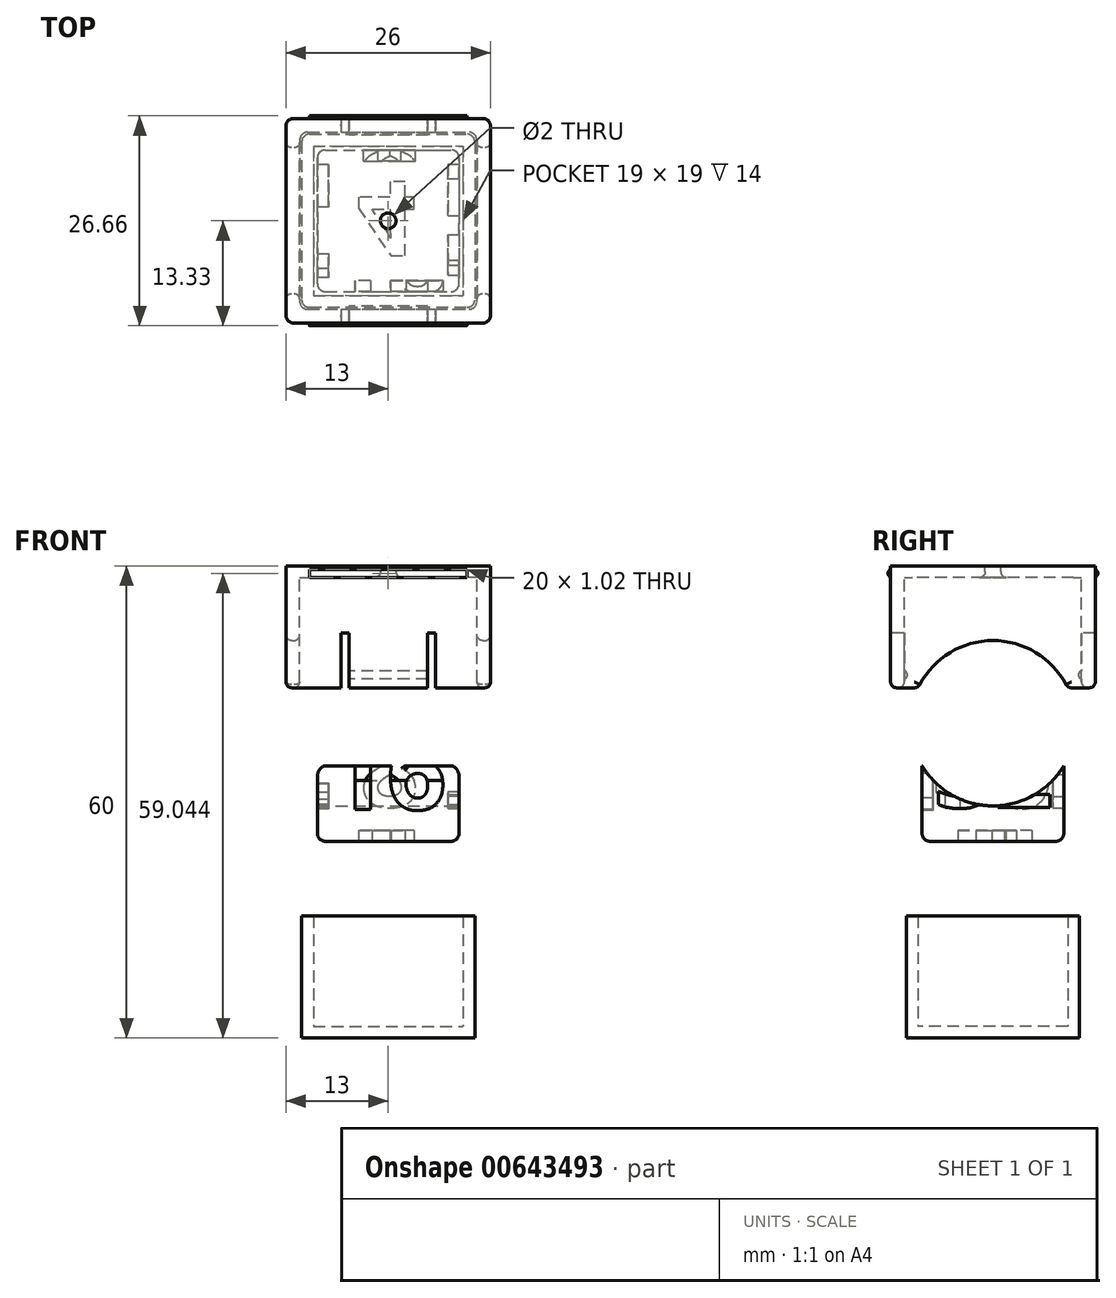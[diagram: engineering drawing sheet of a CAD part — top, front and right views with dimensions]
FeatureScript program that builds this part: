
annotation { "Feature Type Name" : "Feature", "Feature Type Description" : "" }
export const myFeature = defineFeature(function(context is Context, id is Id, definition is map)
    precondition{}
    {
        {
            var Q0;
            Q0=qCreatedBy(makeId("Top.planeOp"),FACE);
            var sketch = newSketch(context, id + "F0", { "sketchPlane" : qUnion([Q0])});
            skLineSegment(sketch, "E0.bottom", {"start": v(-9, 9) * mm, "end": v(9, 9) * mm});
            skLineSegment(sketch, "E0.top", {"start": v(-9, -9) * mm, "end": v(9, -9) * mm});
            skLineSegment(sketch, "E0.left", {"start": v(-9, 9) * mm, "end": v(-9, -9) * mm});
            skLineSegment(sketch, "E0.right", {"start": v(9, 9) * mm, "end": v(9, -9) * mm});
            skSolve(sketch);
        }
        {
            var Q0;
            Q0=makeQuery(id+"F0.imprint","IMPRINT",FACE,{"disambiguationData":[TD([[makeQuery(id+"F0.imprint","IMPRINT",EDGE,{"derivedFrom":sQuery(id+"F0.wireOp",EDGE,"E0.bottom")}),-1.0]])]});
            extrude(context, id + "F1", {"entities" : qUnion([Q0]), "depth" : 18 * mm, "offsetDistance" : 25 * mm});
        }
        {
            var Q0;
            Q0=makeQuery(id+"F1.opExtrude","CAP_FACE",FACE,{"disambiguationData":[OSD([sQuery(id+"F0.wireOp",EDGE,"E0.bottom"),sQuery(id+"F0.wireOp",EDGE,"E0.top"),sQuery(id+"F0.wireOp",EDGE,"E0.left"),sQuery(id+"F0.wireOp",EDGE,"E0.right")])],"isStart":false});
            var sketch = newSketch(context, id + "F2", { "sketchPlane" : qUnion([Q0])});
            skText(sketch, "E1", { "text": "2", "fontName": "Arimo-Bold.ttf"});
            const initialGuessF2  = {"E1": [-0.00386, -0.00431, 1, 0, 0.0095]};
            skSetInitialGuess(sketch, initialGuessF2);
            skSolve(sketch);
        }
        {
            var Q0;
            Q0 = qSketchRegion(id + "F2", true);
            extrude(context, id + "F3", {"entities" : qUnion([Q0]), "operationType" : NewBodyOperationType.REMOVE, "oppositeDirection" : true, "depth" : 1.4 * mm, "offsetDistance" : 25 * mm});
        }
        {
            var Q0;
            Q0=makeQuery(id+"F1.opExtrude","CAP_FACE",FACE,{"disambiguationData":[OSD([sQuery(id+"F0.wireOp",EDGE,"E0.bottom"),sQuery(id+"F0.wireOp",EDGE,"E0.top"),sQuery(id+"F0.wireOp",EDGE,"E0.left"),sQuery(id+"F0.wireOp",EDGE,"E0.right")])],"isStart":true});
            var sketch = newSketch(context, id + "F4", { "sketchPlane" : qUnion([Q0])});
            skText(sketch, "E2", { "text": "4", "fontName": "OpenSans-Bold.ttf"});
            const initialGuessF4  = {"E2": [-0.00403, -0.00496, 1, 0, 0.0095]};
            skSetInitialGuess(sketch, initialGuessF4);
            skSolve(sketch);
        }
        {
            var Q0;
            Q0=makeQuery(id+"F4.imprint","IMPRINT",FACE,{"disambiguationData":[TD([[makeQuery(id+"F4.imprint","IMPRINT",EDGE,{"derivedFrom":sQuery(id+"F4.wireOp",EDGE,"E2.sketch_text.stroke-0")}),-1.0]])]});
            extrude(context, id + "F5", {"entities" : qUnion([Q0]), "operationType" : NewBodyOperationType.REMOVE, "oppositeDirection" : true, "depth" : 1.4 * mm, "offsetDistance" : 25 * mm});
        }
        {
            var Q0;
            Q0=makeQuery(id+"F1.opExtrude","SWEPT_FACE",FACE,{"disambiguationData":[OSD([sQuery(id+"F0.wireOp",EDGE,"E0.bottom")])]});
            var sketch = newSketch(context, id + "F6", { "sketchPlane" : qUnion([Q0])});
            skText(sketch, "E3", { "text": "8", "fontName": "OpenSans-Bold.ttf"});
            const initialGuessF6  = {"E3": [-0.00393, 0.00436, 1, 0, 0.0095]};
            skSetInitialGuess(sketch, initialGuessF6);
            skSolve(sketch);
        }
        {
            var Q0;
            Q0 = qSketchRegion(id + "F6", true);
            extrude(context, id + "F7", {"entities" : qUnion([Q0]), "operationType" : NewBodyOperationType.REMOVE, "oppositeDirection" : true, "depth" : 1.4 * mm, "offsetDistance" : 25 * mm});
        }
        {
            var Q0;
            Q0=makeQuery(id+"F1.opExtrude","SWEPT_FACE",FACE,{"disambiguationData":[OSD([sQuery(id+"F0.wireOp",EDGE,"E0.top")])]});
            var sketch = newSketch(context, id + "F8", { "sketchPlane" : qUnion([Q0])});
            skText(sketch, "E4", { "text": "16", "fontName": "OpenSans-Bold.ttf"});
            const initialGuessF8  = {"E4": [-0.00771, 0.00402, 1, 0, 0.0095]};
            skSetInitialGuess(sketch, initialGuessF8);
            skSolve(sketch);
        }
        {
            var Q0;
            Q0 = qSketchRegion(id + "F8", true);
            extrude(context, id + "F9", {"entities" : qUnion([Q0]), "operationType" : NewBodyOperationType.REMOVE, "oppositeDirection" : true, "depth" : 1.4 * mm, "offsetDistance" : 25 * mm});
        }
        {
            var Q0;
            Q0=makeQuery(id+"F1.opExtrude","SWEPT_FACE",FACE,{"disambiguationData":[OSD([sQuery(id+"F0.wireOp",EDGE,"E0.right")])]});
            var sketch = newSketch(context, id + "F10", { "sketchPlane" : qUnion([Q0])});
            skText(sketch, "E5", { "text": "32", "fontName": "OpenSans-Bold.ttf"});
            const initialGuessF10  = {"E5": [-0.00743, 0.00428, 1, 0, 0.0095]};
            skSetInitialGuess(sketch, initialGuessF10);
            skSolve(sketch);
        }
        {
            var Q0;
            Q0 = qSketchRegion(id + "F10", true);
            extrude(context, id + "F11", {"entities" : qUnion([Q0]), "operationType" : NewBodyOperationType.REMOVE, "oppositeDirection" : true, "depth" : 1.4 * mm, "offsetDistance" : 25 * mm});
        }
        {
            var Q0;
            Q0=makeQuery(id+"F1.opExtrude","SWEPT_FACE",FACE,{"disambiguationData":[OSD([sQuery(id+"F0.wireOp",EDGE,"E0.left")])]});
            var sketch = newSketch(context, id + "F12", { "sketchPlane" : qUnion([Q0])});
            skText(sketch, "E6", { "text": "64", "fontName": "OpenSans-Bold.ttf"});
            const initialGuessF12  = {"E6": [-0.00763, 0.00423, 1, 0, 0.0095]};
            skSetInitialGuess(sketch, initialGuessF12);
            skSolve(sketch);
        }
        {
            var Q0;
            Q0 = qSketchRegion(id + "F12", true);
            extrude(context, id + "F13", {"entities" : qUnion([Q0]), "operationType" : NewBodyOperationType.REMOVE, "oppositeDirection" : true, "depth" : 1.4 * mm, "offsetDistance" : 25 * mm});
        }
        {
            var Q0;
            Q0=makeQuery(id+"F1.opExtrude","CAP_EDGE",EDGE,{"disambiguationData":[OSD([sQuery(id+"F0.wireOp",EDGE,"E0.right")])],"isStart":false});
            var Q1;
            Q1=makeQuery(id+"F1.opExtrude","CAP_EDGE",EDGE,{"disambiguationData":[OSD([sQuery(id+"F0.wireOp",EDGE,"E0.bottom")])],"isStart":false});
            var Q2;
            Q2=makeQuery(id+"F1.opExtrude","SWEPT_EDGE",EDGE,{"disambiguationData":[OSD([sQuery(id+"F0.wireOp",EDGE,"E0.bottom"),sQuery(id+"F0.wireOp",EDGE,"E0.right")])]});
            var Q3;
            Q3=makeQuery(id+"F1.opExtrude","SWEPT_EDGE",EDGE,{"disambiguationData":[OSD([sQuery(id+"F0.wireOp",EDGE,"E0.bottom"),sQuery(id+"F0.wireOp",EDGE,"E0.left")])]});
            var Q4;
            Q4=makeQuery(id+"F1.opExtrude","CAP_EDGE",EDGE,{"disambiguationData":[OSD([sQuery(id+"F0.wireOp",EDGE,"E0.left")])],"isStart":false});
            var Q5;
            Q5=makeQuery(id+"F1.opExtrude","CAP_EDGE",EDGE,{"disambiguationData":[OSD([sQuery(id+"F0.wireOp",EDGE,"E0.top")])],"isStart":false});
            var Q6;
            Q6=makeQuery(id+"F1.opExtrude","SWEPT_EDGE",EDGE,{"disambiguationData":[OSD([sQuery(id+"F0.wireOp",EDGE,"E0.top"),sQuery(id+"F0.wireOp",EDGE,"E0.right")])]});
            var Q7;
            Q7=makeQuery(id+"F1.opExtrude","CAP_EDGE",EDGE,{"disambiguationData":[OSD([sQuery(id+"F0.wireOp",EDGE,"E0.right")])],"isStart":true});
            var Q8;
            Q8=makeQuery(id+"F1.opExtrude","CAP_EDGE",EDGE,{"disambiguationData":[OSD([sQuery(id+"F0.wireOp",EDGE,"E0.top")])],"isStart":true});
            var Q9;
            Q9=makeQuery(id+"F1.opExtrude","SWEPT_EDGE",EDGE,{"disambiguationData":[OSD([sQuery(id+"F0.wireOp",EDGE,"E0.top"),sQuery(id+"F0.wireOp",EDGE,"E0.left")])]});
            var Q10;
            Q10=makeQuery(id+"F1.opExtrude","CAP_EDGE",EDGE,{"disambiguationData":[OSD([sQuery(id+"F0.wireOp",EDGE,"E0.left")])],"isStart":true});
            var Q11;
            Q11=makeQuery(id+"F1.opExtrude","CAP_EDGE",EDGE,{"disambiguationData":[OSD([sQuery(id+"F0.wireOp",EDGE,"E0.bottom")])],"isStart":true});
            fillet(context, id + "F14", {"entities" : qUnion([Q0, Q1, Q2, Q3, Q4, Q5, Q6, Q7, Q8, Q9, Q10, Q11]), "radius" : 1 * mm, "tangentPropagation" : true, "allowEdgeOverflow" : false});
        }
        {
            var Q0;
            Q0=qCreatedBy(makeId("Top.planeOp"),FACE);
            cPlane(context, id + "F15", {"entities" : qUnion([Q0]), "cplaneType" : CPlaneType.OFFSET, "offset" : 25 * mm, "oppositeDirection" : true, "width" : 150 * mm, "height" : 150 * mm});
        }
        {
            var Q0;
            Q0=qCreatedBy(id+"F15.planeOp",FACE);
            var sketch = newSketch(context, id + "F16", { "sketchPlane" : qUnion([Q0])});
            skLineSegment(sketch, "E7.bottom", {"start": v(-11, 11) * mm, "end": v(11, 11) * mm});
            skLineSegment(sketch, "E7.top", {"start": v(-11, -11) * mm, "end": v(11, -11) * mm});
            skLineSegment(sketch, "E7.left", {"start": v(-11, 11) * mm, "end": v(-11, -11) * mm});
            skLineSegment(sketch, "E7.right", {"start": v(11, 11) * mm, "end": v(11, -11) * mm});
            skSolve(sketch);
        }
        {
            var Q0;
            Q0 = qSketchRegion(id + "F16", true);
            extrude(context, id + "F17", {"entities" : qUnion([Q0]), "depth" : 1.5 * mm, "offsetDistance" : 25 * mm});
        }
        {
            var Q0;
            Q0=makeQuery(id+"F17.opExtrude","CAP_FACE",FACE,{"disambiguationData":[OSD([sQuery(id+"F16.wireOp",EDGE,"E7.bottom"),sQuery(id+"F16.wireOp",EDGE,"E7.top"),sQuery(id+"F16.wireOp",EDGE,"E7.left"),sQuery(id+"F16.wireOp",EDGE,"E7.right")])],"isStart":false});
            var sketch = newSketch(context, id + "F18", { "sketchPlane" : qUnion([Q0])});
            skLineSegment(sketch, "E8.bottom", {"start": v(-11, 11) * mm, "end": v(11, 11) * mm});
            skLineSegment(sketch, "E8.top", {"start": v(-11, -11) * mm, "end": v(11, -11) * mm});
            skLineSegment(sketch, "E8.left", {"start": v(-11, 11) * mm, "end": v(-11, -11) * mm});
            skLineSegment(sketch, "E8.right", {"start": v(11, 11) * mm, "end": v(11, -11) * mm});
            skLineSegment(sketch, "E9.bottom", {"start": v(-9.5, 9.5) * mm, "end": v(9.5, 9.5) * mm});
            skLineSegment(sketch, "E9.top", {"start": v(-9.5, -9.5) * mm, "end": v(9.5, -9.5) * mm});
            skLineSegment(sketch, "E9.left", {"start": v(-9.5, 9.5) * mm, "end": v(-9.5, -9.5) * mm});
            skLineSegment(sketch, "E9.right", {"start": v(9.5, 9.5) * mm, "end": v(9.5, -9.5) * mm});
            skSolve(sketch);
        }
        {
            var Q0;
            Q0 = qSketchRegion(id + "F18", true);
            extrude(context, id + "F19", {"entities" : qUnion([Q0]), "operationType" : NewBodyOperationType.ADD, "depth" : 14 * mm, "offsetDistance" : 25 * mm});
        }
        {
            var Q0;
            Q0=makeQuery(id+"F19.boolean.opBoolean","MERGE",EDGE,{"derivedFrom":[makeQuery(id+"F17.opExtrude","SWEPT_EDGE",EDGE,{"disambiguationData":[OSD([sQuery(id+"F16.wireOp",EDGE,"E7.bottom"),sQuery(id+"F16.wireOp",EDGE,"E7.left")])]}),makeQuery(id+"F19.opExtrude","SWEPT_EDGE",EDGE,{"disambiguationData":[OSD([sQuery(id+"F18.wireOp",EDGE,"E8.bottom"),sQuery(id+"F18.wireOp",EDGE,"E8.left")])]})]});
            var Q1;
            Q1=makeQuery(id+"F19.boolean.opBoolean","MERGE",EDGE,{"derivedFrom":[makeQuery(id+"F17.opExtrude","SWEPT_EDGE",EDGE,{"disambiguationData":[OSD([sQuery(id+"F16.wireOp",EDGE,"E7.bottom"),sQuery(id+"F16.wireOp",EDGE,"E7.right")])]}),makeQuery(id+"F19.opExtrude","SWEPT_EDGE",EDGE,{"disambiguationData":[OSD([sQuery(id+"F18.wireOp",EDGE,"E8.bottom"),sQuery(id+"F18.wireOp",EDGE,"E8.right")])]})]});
            var Q2;
            Q2=makeQuery(id+"F19.boolean.opBoolean","MERGE",EDGE,{"derivedFrom":[makeQuery(id+"F17.opExtrude","SWEPT_EDGE",EDGE,{"disambiguationData":[OSD([sQuery(id+"F16.wireOp",EDGE,"E7.top"),sQuery(id+"F16.wireOp",EDGE,"E7.right")])]}),makeQuery(id+"F19.opExtrude","SWEPT_EDGE",EDGE,{"disambiguationData":[OSD([sQuery(id+"F18.wireOp",EDGE,"E8.top"),sQuery(id+"F18.wireOp",EDGE,"E8.right")])]})]});
            var Q3;
            Q3=makeQuery(id+"F19.boolean.opBoolean","MERGE",EDGE,{"derivedFrom":[makeQuery(id+"F17.opExtrude","SWEPT_EDGE",EDGE,{"disambiguationData":[OSD([sQuery(id+"F16.wireOp",EDGE,"E7.top"),sQuery(id+"F16.wireOp",EDGE,"E7.left")])]}),makeQuery(id+"F19.opExtrude","SWEPT_EDGE",EDGE,{"disambiguationData":[OSD([sQuery(id+"F18.wireOp",EDGE,"E8.top"),sQuery(id+"F18.wireOp",EDGE,"E8.left")])]})]});
            fillet(context, id + "F20", {"entities" : qUnion([Q0, Q1, Q2, Q3]), "radius" : 1 * mm, "tangentPropagation" : true, "allowEdgeOverflow" : false});
        }
        {
            var Q0;
            Q0=qCreatedBy(makeId("Top.planeOp"),FACE);
            cPlane(context, id + "F21", {"entities" : qUnion([Q0]), "cplaneType" : CPlaneType.OFFSET, "offset" : 35 * mm, "width" : 150 * mm, "height" : 150 * mm});
        }
        {
            var Q0;
            Q0=qCreatedBy(id+"F21.planeOp",FACE);
            var sketch = newSketch(context, id + "F22", { "sketchPlane" : qUnion([Q0])});
            skLineSegment(sketch, "E10.bottom", {"start": v(-13, 13) * mm, "end": v(13, 13) * mm});
            skLineSegment(sketch, "E10.top", {"start": v(-13, -13) * mm, "end": v(13, -13) * mm});
            skLineSegment(sketch, "E10.left", {"start": v(-13, 13) * mm, "end": v(-13, -13) * mm});
            skLineSegment(sketch, "E10.right", {"start": v(13, 13) * mm, "end": v(13, -13) * mm});
            skSolve(sketch);
        }
        {
            var Q0;
            Q0 = qSketchRegion(id + "F22", true);
            extrude(context, id + "F23", {"entities" : qUnion([Q0]), "oppositeDirection" : true, "depth" : 1.5 * mm, "offsetDistance" : 25 * mm});
        }
        {
            var Q0;
            Q0=makeQuery(id+"F23.opExtrude","CAP_FACE",FACE,{"disambiguationData":[OSD([sQuery(id+"F22.wireOp",EDGE,"E10.bottom"),sQuery(id+"F22.wireOp",EDGE,"E10.top"),sQuery(id+"F22.wireOp",EDGE,"E10.left"),sQuery(id+"F22.wireOp",EDGE,"E10.right")])],"isStart":false});
            var sketch = newSketch(context, id + "F24", { "sketchPlane" : qUnion([Q0])});
            skLineSegment(sketch, "E11.bottom", {"start": v(-13, -13) * mm, "end": v(13, -13) * mm});
            skLineSegment(sketch, "E11.top", {"start": v(-13, 13) * mm, "end": v(13, 13) * mm});
            skLineSegment(sketch, "E11.left", {"start": v(-13, -13) * mm, "end": v(-13, 13) * mm});
            skLineSegment(sketch, "E11.right", {"start": v(13, -13) * mm, "end": v(13, 13) * mm});
            skLineSegment(sketch, "E12.bottom", {"start": v(-11.25, -11.25) * mm, "end": v(11.25, -11.25) * mm});
            skLineSegment(sketch, "E12.top", {"start": v(-11.25, 11.25) * mm, "end": v(11.25, 11.25) * mm});
            skLineSegment(sketch, "E12.left", {"start": v(-11.25, -11.25) * mm, "end": v(-11.25, 11.25) * mm});
            skLineSegment(sketch, "E12.right", {"start": v(11.25, -11.25) * mm, "end": v(11.25, 11.25) * mm});
            skSolve(sketch);
        }
        {
            var Q0;
            Q0 = qSketchRegion(id + "F24", true);
            extrude(context, id + "F25", {"entities" : qUnion([Q0]), "operationType" : NewBodyOperationType.ADD, "depth" : 14 * mm, "offsetDistance" : 25 * mm});
        }
        {
            var Q0;
            Q0=makeQuery(id+"F25.opExtrude","SWEPT_EDGE",EDGE,{"disambiguationData":[OSD([sQuery(id+"F24.wireOp",EDGE,"E12.top"),sQuery(id+"F24.wireOp",EDGE,"E12.left")])]});
            var Q1;
            Q1=makeQuery(id+"F25.opExtrude","SWEPT_EDGE",EDGE,{"disambiguationData":[OSD([sQuery(id+"F24.wireOp",EDGE,"E12.top"),sQuery(id+"F24.wireOp",EDGE,"E12.right")])]});
            var Q2;
            Q2=makeQuery(id+"F25.opExtrude","SWEPT_EDGE",EDGE,{"disambiguationData":[OSD([sQuery(id+"F24.wireOp",EDGE,"E12.bottom"),sQuery(id+"F24.wireOp",EDGE,"E12.left")])]});
            var Q3;
            Q3=makeQuery(id+"F25.opExtrude","SWEPT_EDGE",EDGE,{"disambiguationData":[OSD([sQuery(id+"F24.wireOp",EDGE,"E12.bottom"),sQuery(id+"F24.wireOp",EDGE,"E12.right")])]});
            var Q4;
            Q4=makeQuery(id+"F25.boolean.opBoolean","MERGE",EDGE,{"derivedFrom":[makeQuery(id+"F23.opExtrude","SWEPT_EDGE",EDGE,{"disambiguationData":[OSD([sQuery(id+"F22.wireOp",EDGE,"E10.top"),sQuery(id+"F22.wireOp",EDGE,"E10.right")])]}),makeQuery(id+"F25.opExtrude","SWEPT_EDGE",EDGE,{"disambiguationData":[OSD([sQuery(id+"F24.wireOp",EDGE,"E11.top"),sQuery(id+"F24.wireOp",EDGE,"E11.right")])]})]});
            var Q5;
            Q5=makeQuery(id+"F25.boolean.opBoolean","MERGE",EDGE,{"derivedFrom":[makeQuery(id+"F23.opExtrude","SWEPT_EDGE",EDGE,{"disambiguationData":[OSD([sQuery(id+"F22.wireOp",EDGE,"E10.top"),sQuery(id+"F22.wireOp",EDGE,"E10.left")])]}),makeQuery(id+"F25.opExtrude","SWEPT_EDGE",EDGE,{"disambiguationData":[OSD([sQuery(id+"F24.wireOp",EDGE,"E11.top"),sQuery(id+"F24.wireOp",EDGE,"E11.left")])]})]});
            var Q6;
            Q6=makeQuery(id+"F25.boolean.opBoolean","MERGE",EDGE,{"derivedFrom":[makeQuery(id+"F23.opExtrude","SWEPT_EDGE",EDGE,{"disambiguationData":[OSD([sQuery(id+"F22.wireOp",EDGE,"E10.bottom"),sQuery(id+"F22.wireOp",EDGE,"E10.left")])]}),makeQuery(id+"F25.opExtrude","SWEPT_EDGE",EDGE,{"disambiguationData":[OSD([sQuery(id+"F24.wireOp",EDGE,"E11.bottom"),sQuery(id+"F24.wireOp",EDGE,"E11.left")])]})]});
            var Q7;
            Q7=makeQuery(id+"F25.boolean.opBoolean","MERGE",EDGE,{"derivedFrom":[makeQuery(id+"F23.opExtrude","SWEPT_EDGE",EDGE,{"disambiguationData":[OSD([sQuery(id+"F22.wireOp",EDGE,"E10.bottom"),sQuery(id+"F22.wireOp",EDGE,"E10.right")])]}),makeQuery(id+"F25.opExtrude","SWEPT_EDGE",EDGE,{"disambiguationData":[OSD([sQuery(id+"F24.wireOp",EDGE,"E11.bottom"),sQuery(id+"F24.wireOp",EDGE,"E11.right")])]})]});
            fillet(context, id + "F26", {"entities" : qUnion([Q0, Q1, Q2, Q3, Q4, Q5, Q6, Q7]), "radius" : 1 * mm, "tangentPropagation" : true, "allowEdgeOverflow" : false});
        }
        {
            var Q0;
            Q0=qCreatedBy(makeId("Right.planeOp"),FACE);
            var sketch = newSketch(context, id + "F27", { "sketchPlane" : qUnion([Q0])});
            skCircle(sketch, "E13", {"center": v(0, 15) * mm, "radius": 10.5 * mm});
            skSolve(sketch);
        }
        {
            var Q0;
            Q0 = qSketchRegion(id + "F27", true);
            extrude(context, id + "F28", {"entities" : qUnion([Q0]), "operationType" : NewBodyOperationType.REMOVE, "endBound" : BoundingType.SYMMETRIC, "oppositeDirection" : true, "depth" : 30 * mm, "offsetDistance" : 25 * mm});
        }
        {
            var Q0;
            Q0=makeQuery(id+"F28.boolean.opBoolean","INTERSECT",EDGE,{"derivedFrom":[makeQuery(id+"F25.boolean.opBoolean","MERGE",FACE,{"derivedFrom":[makeQuery(id+"F23.opExtrude","SWEPT_FACE",FACE,{"disambiguationData":[OSD([sQuery(id+"F22.wireOp",EDGE,"E10.right")])]}),makeQuery(id+"F25.opExtrude","SWEPT_FACE",FACE,{"disambiguationData":[OSD([sQuery(id+"F24.wireOp",EDGE,"E11.right")])]})]}),makeQuery(id+"F28.opExtrude","SWEPT_FACE",FACE,{"disambiguationData":[OSD([sQuery(id+"F27.wireOp",EDGE,"E13")])]})]});
            var Q1;
            Q1=makeQuery(id+"F28.boolean.opBoolean","INTERSECT",EDGE,{"derivedFrom":[makeQuery(id+"F25.opExtrude","SWEPT_FACE",FACE,{"disambiguationData":[OSD([sQuery(id+"F24.wireOp",EDGE,"E12.right")])]}),makeQuery(id+"F28.opExtrude","SWEPT_FACE",FACE,{"disambiguationData":[OSD([sQuery(id+"F27.wireOp",EDGE,"E13")])]})]});
            var Q2;
            Q2=makeQuery(id+"F28.boolean.opBoolean","INTERSECT",EDGE,{"derivedFrom":[makeQuery(id+"F25.boolean.opBoolean","MERGE",FACE,{"derivedFrom":[makeQuery(id+"F23.opExtrude","SWEPT_FACE",FACE,{"disambiguationData":[OSD([sQuery(id+"F22.wireOp",EDGE,"E10.left")])]}),makeQuery(id+"F25.opExtrude","SWEPT_FACE",FACE,{"disambiguationData":[OSD([sQuery(id+"F24.wireOp",EDGE,"E11.left")])]})]}),makeQuery(id+"F28.opExtrude","SWEPT_FACE",FACE,{"disambiguationData":[OSD([sQuery(id+"F27.wireOp",EDGE,"E13")])]})]});
            var Q3;
            Q3=makeQuery(id+"F28.boolean.opBoolean","INTERSECT",EDGE,{"derivedFrom":[makeQuery(id+"F25.opExtrude","SWEPT_FACE",FACE,{"disambiguationData":[OSD([sQuery(id+"F24.wireOp",EDGE,"E12.left")])]}),makeQuery(id+"F28.opExtrude","SWEPT_FACE",FACE,{"disambiguationData":[OSD([sQuery(id+"F27.wireOp",EDGE,"E13")])]})]});
            fillet(context, id + "F29", {"entities" : qUnion([Q0, Q1, Q2, Q3]), "radius" : 0.74 * mm, "tangentPropagation" : true, "allowEdgeOverflow" : false});
        }
        {
            var Q0;
            Q0=makeQuery(id+"F23.opExtrude","CAP_FACE",FACE,{"disambiguationData":[OSD([sQuery(id+"F22.wireOp",EDGE,"E10.bottom"),sQuery(id+"F22.wireOp",EDGE,"E10.top"),sQuery(id+"F22.wireOp",EDGE,"E10.left"),sQuery(id+"F22.wireOp",EDGE,"E10.right")])],"isStart":true});
            var sketch = newSketch(context, id + "F30", { "sketchPlane" : qUnion([Q0])});
            skCircle(sketch, "E14", {"center": v(0, 0) * mm, "radius": 1 * mm});
            skSolve(sketch);
        }
        {
            var Q0;
            Q0 = qSketchRegion(id + "F30", true);
            extrude(context, id + "F31", {"entities" : qUnion([Q0]), "operationType" : NewBodyOperationType.REMOVE, "oppositeDirection" : true, "depth" : 3 * mm, "offsetDistance" : 25 * mm});
        }
        {
            var Q0;
            Q0=qCreatedBy(makeId("Right.planeOp"),FACE);
            var sketch = newSketch(context, id + "F32", { "sketchPlane" : qUnion([Q0])});
            skArc(sketch, "E15", {"start": v(11.25, 21.63) * mm, "mid": v(10.85, 21.13) * mm, "end": v(11.25, 20.62) * mm});
            skLineSegment(sketch, "E16", {"start": v(11.25, 17.44) * mm, "end": v(11.25, 26.73) * mm, "construction": true});
            skLineSegment(sketch, "E17", {"start": v(11.25, 21.63) * mm, "end": v(11.25, 20.62) * mm});
            skSolve(sketch);
        }
        {
            var Q0;
            Q0 = qSketchRegion(id + "F32", true);
            extrude(context, id + "F33", {"entities" : qUnion([Q0]), "endBound" : BoundingType.SYMMETRIC, "depth" : 10 * mm, "offsetDistance" : 25 * mm});
        }
        {
            var Q0;
            Q0=makeQuery(id+"F33.opExtrude","SWEPT_BODY",BODY,{"disambiguationData":[OSD([sQuery(id+"F32.wireOp",EDGE,"E15"),sQuery(id+"F32.wireOp",EDGE,"E17")])]});
            var Q1;
            Q1=qCreatedBy(makeId("Front.planeOp"),FACE);
            mirror(context, id + "F34", {"operationType" : NewBodyOperationType.ADD, "entities" : qUnion([Q0]), "mirrorPlane" : qUnion([Q1])});
        }
        {
            var Q0;
            Q0=makeQuery(id+"F25.opExtrude","SWEPT_FACE",FACE,{"disambiguationData":[OSD([sQuery(id+"F24.wireOp",EDGE,"E12.top")])]});
            var sketch = newSketch(context, id + "F35", { "sketchPlane" : qUnion([Q0])});
            skLineSegment(sketch, "E18.bottom", {"start": v(-5, 16.34) * mm, "end": v(-6, 16.34) * mm});
            skLineSegment(sketch, "E18.top", {"start": v(-5, 26.45) * mm, "end": v(-6, 26.45) * mm});
            skLineSegment(sketch, "E18.left", {"start": v(-5, 16.34) * mm, "end": v(-5, 26.45) * mm});
            skLineSegment(sketch, "E18.right", {"start": v(-6, 16.34) * mm, "end": v(-6, 26.45) * mm});
            skSolve(sketch);
        }
        {
            var Q0;
            Q0 = qSketchRegion(id + "F35", true);
            extrude(context, id + "F36", {"entities" : qUnion([Q0]), "endBound" : BoundingType.SYMMETRIC, "depth" : 50 * mm, "offsetDistance" : 25 * mm});
        }
        {
            var Q0;
            Q0=makeQuery(id+"F36.opExtrude","SWEPT_BODY",BODY,{"disambiguationData":[OSD([sQuery(id+"F35.wireOp",EDGE,"E18.bottom"),sQuery(id+"F35.wireOp",EDGE,"E18.top"),sQuery(id+"F35.wireOp",EDGE,"E18.left"),sQuery(id+"F35.wireOp",EDGE,"E18.right")])]});
            var Q1;
            Q1=qCreatedBy(makeId("Right.planeOp"),FACE);
            mirror(context, id + "F37", {"entities" : qUnion([Q0]), "mirrorPlane" : qUnion([Q1])});
        }
        {
            var Q0;
            Q0=makeQuery(id+"F36.opExtrude","SWEPT_BODY",BODY,{"disambiguationData":[OSD([sQuery(id+"F35.wireOp",EDGE,"E18.bottom"),sQuery(id+"F35.wireOp",EDGE,"E18.top"),sQuery(id+"F35.wireOp",EDGE,"E18.left"),sQuery(id+"F35.wireOp",EDGE,"E18.right")])]});
            var Q1;
            Q1=makeQuery(id+"F37.opPattern","COPY",BODY,{"derivedFrom":makeQuery(id+"F36.opExtrude","SWEPT_BODY",BODY,{"disambiguationData":[OSD([sQuery(id+"F35.wireOp",EDGE,"E18.bottom"),sQuery(id+"F35.wireOp",EDGE,"E18.top"),sQuery(id+"F35.wireOp",EDGE,"E18.left"),sQuery(id+"F35.wireOp",EDGE,"E18.right")])]}),"instanceName":"1"});
            var Q2;
            Q2=makeQuery(id+"F23.opExtrude","SWEPT_BODY",BODY,{"disambiguationData":[OSD([sQuery(id+"F22.wireOp",EDGE,"E10.bottom"),sQuery(id+"F22.wireOp",EDGE,"E10.top"),sQuery(id+"F22.wireOp",EDGE,"E10.left"),sQuery(id+"F22.wireOp",EDGE,"E10.right")])]});
            booleanBodies(context, id + "F38", {"operationType" : BooleanOperationType.SUBTRACTION, "tools" : qUnion([Q0, Q1]), "targets" : qUnion([Q2])});
        }
        {
            var Q0;
            Q0=qCreatedBy(makeId("Right.planeOp"),FACE);
            var sketch = newSketch(context, id + "F39", { "sketchPlane" : qUnion([Q0])});
            skArc(sketch, "E19", {"start": v(-13, 34.55) * mm, "mid": v(-13.33, 34.04) * mm, "end": v(-13, 33.54) * mm});
            skLineSegment(sketch, "E20", {"start": v(-13, 36) * mm, "end": v(-13, 28.95) * mm, "construction": true});
            skLineSegment(sketch, "E21", {"start": v(-13, 34.55) * mm, "end": v(-13, 33.54) * mm});
            skSolve(sketch);
        }
        {
            var Q0;
            Q0 = qSketchRegion(id + "F39", true);
            extrude(context, id + "F40", {"entities" : qUnion([Q0]), "endBound" : BoundingType.SYMMETRIC, "depth" : 20 * mm, "offsetDistance" : 25 * mm});
        }
        {
            var Q0;
            Q0=makeQuery(id+"F40.opExtrude","SWEPT_BODY",BODY,{"disambiguationData":[OSD([sQuery(id+"F39.wireOp",EDGE,"E19"),sQuery(id+"F39.wireOp",EDGE,"E21")])]});
            var Q1;
            Q1=qCreatedBy(makeId("Front.planeOp"),FACE);
            mirror(context, id + "F41", {"operationType" : NewBodyOperationType.ADD, "entities" : qUnion([Q0]), "mirrorPlane" : qUnion([Q1])});
        }
        {
            var Q0;
            {var subQ0=sQuery(id+"F24.wireOp",EDGE,"E12.left");var subQ1=sQuery(id+"F24.wireOp",EDGE,"E12.bottom");Q0=makeQuery(id+"F26.opFillet","BLEND_EDGE",EDGE,{"blendedFrom":[makeQuery(id+"F25.opExtrude","SWEPT_EDGE",EDGE,{"disambiguationData":[OSD([subQ1,subQ0])]}),makeQuery(id+"F25.opExtrude","CAP_FACE",FACE,{"disambiguationData":[OSD([sQuery(id+"F24.wireOp",EDGE,"E11.bottom"),sQuery(id+"F24.wireOp",EDGE,"E11.top"),sQuery(id+"F24.wireOp",EDGE,"E11.left"),sQuery(id+"F24.wireOp",EDGE,"E11.right"),subQ1,sQuery(id+"F24.wireOp",EDGE,"E12.top"),subQ0,sQuery(id+"F24.wireOp",EDGE,"E12.right")])],"isStart":false})],"blendedInto":[makeQuery(id+"F25.opExtrude","CAP_FACE",FACE,{"disambiguationData":[OSD([sQuery(id+"F24.wireOp",EDGE,"E11.bottom"),sQuery(id+"F24.wireOp",EDGE,"E11.top"),sQuery(id+"F24.wireOp",EDGE,"E11.left"),sQuery(id+"F24.wireOp",EDGE,"E11.right"),subQ1,sQuery(id+"F24.wireOp",EDGE,"E12.top"),subQ0,sQuery(id+"F24.wireOp",EDGE,"E12.right")])],"isStart":false})]});}
            var Q1;
            {var subQ2=sQuery(id+"F24.wireOp",EDGE,"E12.bottom");var subQ3=makeQuery(id+"F36.opExtrude","SWEPT_FACE",FACE,{"disambiguationData":[OSD([sQuery(id+"F35.wireOp",EDGE,"E18.left")])]});Q1=makeQuery(id+"F38.opBoolean","SPLIT",EDGE,{"disambiguationData":[TD([subQ3])],"derivedFrom":makeQuery(id+"F25.opExtrude","CAP_EDGE",EDGE,{"disambiguationData":[OSD([subQ2])],"isStart":false})});}
            var Q2;
            {var subQ2=sQuery(id+"F24.wireOp",EDGE,"E11.bottom");var subQ3=makeQuery(id+"F36.opExtrude","SWEPT_FACE",FACE,{"disambiguationData":[OSD([sQuery(id+"F35.wireOp",EDGE,"E18.left")])]});Q2=makeQuery(id+"F38.opBoolean","SPLIT",EDGE,{"disambiguationData":[TD([subQ3])],"derivedFrom":makeQuery(id+"F25.opExtrude","CAP_EDGE",EDGE,{"disambiguationData":[OSD([subQ2])],"isStart":false})});}
            var Q3;
            {var subQ0=sQuery(id+"F24.wireOp",EDGE,"E11.bottom");Q3=makeQuery(id+"F38.opBoolean","SPLIT",EDGE,{"disambiguationData":[TD([makeQuery(id+"F36.opExtrude","SWEPT_FACE",FACE,{"disambiguationData":[OSD([sQuery(id+"F35.wireOp",EDGE,"E18.right")])]})])],"derivedFrom":makeQuery(id+"F25.opExtrude","CAP_EDGE",EDGE,{"disambiguationData":[OSD([subQ0])],"isStart":false})});}
            var Q4;
            {var subQ0=sQuery(id+"F24.wireOp",EDGE,"E12.right");var subQ1=sQuery(id+"F24.wireOp",EDGE,"E12.top");Q4=makeQuery(id+"F26.opFillet","BLEND_EDGE",EDGE,{"blendedFrom":[makeQuery(id+"F25.opExtrude","SWEPT_EDGE",EDGE,{"disambiguationData":[OSD([subQ1,subQ0])]}),makeQuery(id+"F25.opExtrude","CAP_FACE",FACE,{"disambiguationData":[OSD([sQuery(id+"F24.wireOp",EDGE,"E11.bottom"),sQuery(id+"F24.wireOp",EDGE,"E11.top"),sQuery(id+"F24.wireOp",EDGE,"E11.left"),sQuery(id+"F24.wireOp",EDGE,"E11.right"),sQuery(id+"F24.wireOp",EDGE,"E12.bottom"),subQ1,sQuery(id+"F24.wireOp",EDGE,"E12.left"),subQ0])],"isStart":false})],"blendedInto":[makeQuery(id+"F25.opExtrude","CAP_FACE",FACE,{"disambiguationData":[OSD([sQuery(id+"F24.wireOp",EDGE,"E11.bottom"),sQuery(id+"F24.wireOp",EDGE,"E11.top"),sQuery(id+"F24.wireOp",EDGE,"E11.left"),sQuery(id+"F24.wireOp",EDGE,"E11.right"),sQuery(id+"F24.wireOp",EDGE,"E12.bottom"),subQ1,sQuery(id+"F24.wireOp",EDGE,"E12.left"),subQ0])],"isStart":false})]});}
            var Q5;
            {var subQ2=sQuery(id+"F24.wireOp",EDGE,"E11.top");var subQ3=makeQuery(id+"F36.opExtrude","SWEPT_FACE",FACE,{"disambiguationData":[OSD([sQuery(id+"F35.wireOp",EDGE,"E18.left")])]});Q5=makeQuery(id+"F38.opBoolean","SPLIT",EDGE,{"disambiguationData":[TD([subQ3])],"derivedFrom":makeQuery(id+"F25.opExtrude","CAP_EDGE",EDGE,{"disambiguationData":[OSD([subQ2])],"isStart":false})});}
            var Q6;
            {var subQ0=sQuery(id+"F24.wireOp",EDGE,"E12.left");var subQ1=sQuery(id+"F24.wireOp",EDGE,"E12.top");Q6=makeQuery(id+"F26.opFillet","BLEND_EDGE",EDGE,{"blendedFrom":[makeQuery(id+"F25.opExtrude","SWEPT_EDGE",EDGE,{"disambiguationData":[OSD([subQ1,subQ0])]}),makeQuery(id+"F25.opExtrude","CAP_FACE",FACE,{"disambiguationData":[OSD([sQuery(id+"F24.wireOp",EDGE,"E11.bottom"),sQuery(id+"F24.wireOp",EDGE,"E11.top"),sQuery(id+"F24.wireOp",EDGE,"E11.left"),sQuery(id+"F24.wireOp",EDGE,"E11.right"),sQuery(id+"F24.wireOp",EDGE,"E12.bottom"),subQ1,subQ0,sQuery(id+"F24.wireOp",EDGE,"E12.right")])],"isStart":false})],"blendedInto":[makeQuery(id+"F25.opExtrude","CAP_FACE",FACE,{"disambiguationData":[OSD([sQuery(id+"F24.wireOp",EDGE,"E11.bottom"),sQuery(id+"F24.wireOp",EDGE,"E11.top"),sQuery(id+"F24.wireOp",EDGE,"E11.left"),sQuery(id+"F24.wireOp",EDGE,"E11.right"),sQuery(id+"F24.wireOp",EDGE,"E12.bottom"),subQ1,subQ0,sQuery(id+"F24.wireOp",EDGE,"E12.right")])],"isStart":false})]});}
            var Q7;
            {var subQ2=sQuery(id+"F24.wireOp",EDGE,"E12.top");var subQ3=makeQuery(id+"F36.opExtrude","SWEPT_FACE",FACE,{"disambiguationData":[OSD([sQuery(id+"F35.wireOp",EDGE,"E18.left")])]});Q7=makeQuery(id+"F38.opBoolean","SPLIT",EDGE,{"disambiguationData":[TD([subQ3])],"derivedFrom":makeQuery(id+"F25.opExtrude","CAP_EDGE",EDGE,{"disambiguationData":[OSD([subQ2])],"isStart":false})});}
            var Q8;
            Q8=makeQuery(id+"F31.boolean.opBoolean","INTERSECT",EDGE,{"derivedFrom":[makeQuery(id+"F23.opExtrude","CAP_FACE",FACE,{"disambiguationData":[OSD([sQuery(id+"F22.wireOp",EDGE,"E10.bottom"),sQuery(id+"F22.wireOp",EDGE,"E10.top"),sQuery(id+"F22.wireOp",EDGE,"E10.left"),sQuery(id+"F22.wireOp",EDGE,"E10.right")])],"isStart":false}),makeQuery(id+"F31.opExtrude","SWEPT_FACE",FACE,{"disambiguationData":[OSD([sQuery(id+"F30.wireOp",EDGE,"E14")])]})]});
            fillet(context, id + "F42", {"entities" : qUnion([Q0, Q1, Q2, Q3, Q4, Q5, Q6, Q7, Q8]), "radius" : 0.74 * mm, "tangentPropagation" : true, "allowEdgeOverflow" : false});
        }
    });
